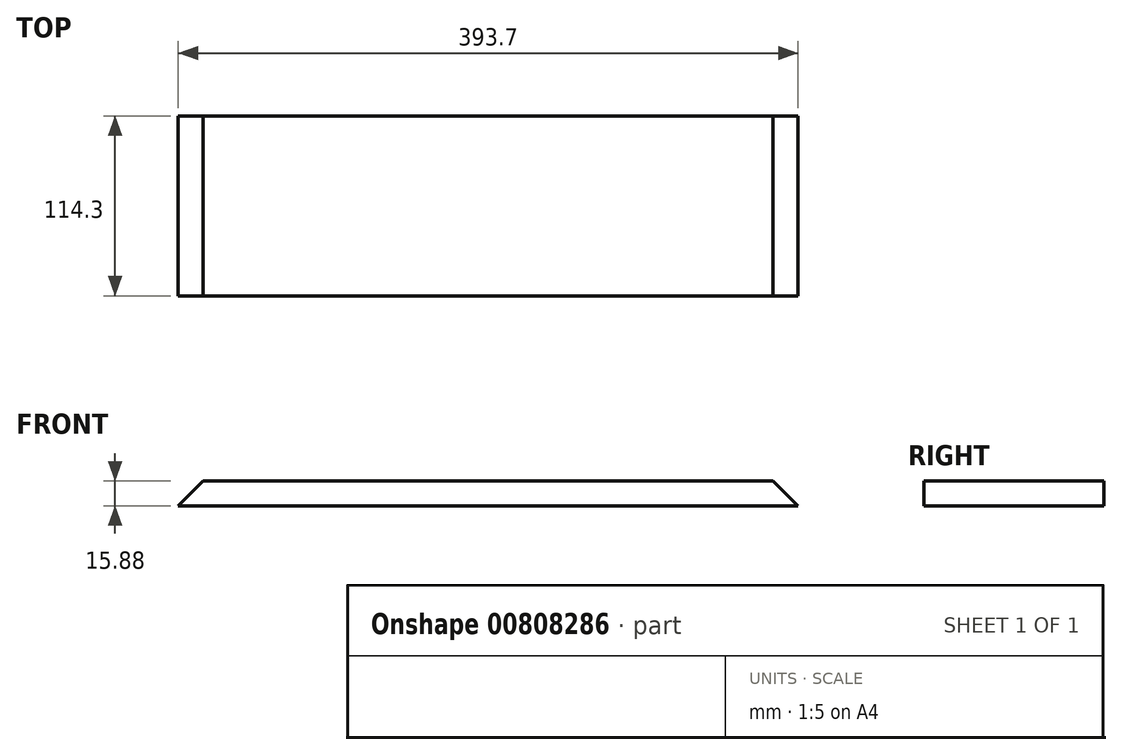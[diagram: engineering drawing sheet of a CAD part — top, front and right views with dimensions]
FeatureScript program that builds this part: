
annotation { "Feature Type Name" : "Feature", "Feature Type Description" : "" }
export const myFeature = defineFeature(function(context is Context, id is Id, definition is map)
    precondition{}
    {
        {
            var Q0;
            Q0=qCreatedBy(makeId("Top.planeOp"),FACE);
            var sketch = newSketch(context, id + "F0", { "sketchPlane" : qUnion([Q0])});
            skLineSegment(sketch, "E0.bottom", {"start": v(196.85, -57.15) * mm, "end": v(-196.85, -57.15) * mm});
            skLineSegment(sketch, "E0.top", {"start": v(196.85, 57.15) * mm, "end": v(-196.85, 57.15) * mm});
            skLineSegment(sketch, "E0.left", {"start": v(196.85, -57.15) * mm, "end": v(196.85, 57.15) * mm});
            skLineSegment(sketch, "E0.right", {"start": v(-196.85, -57.15) * mm, "end": v(-196.85, 57.15) * mm});
            skPoint(sketch, "E0.middle", {"position": v(0, 0) * mm});
            skSolve(sketch);
        }
        {
            var Q0;
            Q0=qSketchRegion(id+"F0",true);
            extrude(context, id + "F1", {"entities" : qUnion([Q0]), "depth" : 15.88 * mm, "offsetDistance" : 25 * mm});
        }
        {
            var Q0;
            Q0=makeQuery(id+"F1.opExtrude","SWEPT_FACE",FACE,{"disambiguationData":[OSD([sQuery(id+"F0.wireOp",EDGE,"E0.bottom")])]});
            var sketch = newSketch(context, id + "F2", { "sketchPlane" : qUnion([Q0])});
            skLineSegment(sketch, "E1", {"start": v(-196.85, 0) * mm, "end": v(-180.98, 15.88) * mm});
            skLineSegment(sketch, "E2", {"start": v(-180.98, 15.88) * mm, "end": v(-180.98, 49.05) * mm});
            skLineSegment(sketch, "E3", {"start": v(-180.98, 49.05) * mm, "end": v(-226.02, 49.05) * mm});
            skLineSegment(sketch, "E4", {"start": v(-226.02, 49.05) * mm, "end": v(-226.02, 0) * mm});
            skLineSegment(sketch, "E5", {"start": v(-226.02, 0) * mm, "end": v(-196.85, 0) * mm});
            skLineSegment(sketch, "E6.0", {"start": v(196.85, 15.88) * mm, "end": v(-196.85, 15.88) * mm, "construction": true});
            skLineSegment(sketch, "E7", {"start": v(0, 15.88) * mm, "end": v(0, 70.31) * mm, "construction": true});
            skLineSegment(sketch, "E8.MirrorCS", {"start": v(180.98, 49.05) * mm, "end": v(226.02, 49.05) * mm});
            skLineSegment(sketch, "E9.MirrorCS", {"start": v(226.02, 0) * mm, "end": v(196.85, 0) * mm});
            skLineSegment(sketch, "E10.MirrorCS", {"start": v(226.02, 49.05) * mm, "end": v(226.02, 0) * mm});
            skLineSegment(sketch, "E11.MirrorCS", {"start": v(196.85, 0) * mm, "end": v(180.98, 15.88) * mm});
            skLineSegment(sketch, "E12.MirrorCS", {"start": v(180.98, 15.88) * mm, "end": v(180.98, 49.05) * mm});
            skSolve(sketch);
        }
        {
            var Q0;
            Q0=qSketchRegion(id+"F2",true);
            extrude(context, id + "F3", {"entities" : qUnion([Q0]), "operationType" : NewBodyOperationType.REMOVE, "endBound" : BoundingType.THROUGH_ALL, "oppositeDirection" : true, "depth" : 25.4 * mm, "offsetDistance" : 25.4 * mm});
        }
    });
